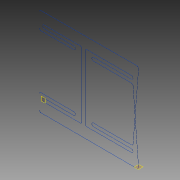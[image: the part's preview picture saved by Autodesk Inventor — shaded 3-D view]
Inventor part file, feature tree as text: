
AUTODESK INVENTOR PART (.ipt)
format: ipt  version: 2013 (Build 170138000, 138)  size: 158,208 bytes
history: native  units: in
note: dims shown in document units (in); Inventor stores cm internally (conversion verified against a paired STEP export)
features: reference x20, sketch x3, plane x2, sweep x1, extrude x1
ambient origin geometry x8: Origin, YZ Plane, XZ Plane, XY Plane, X Axis, Y Axis, Z Axis, Center Point
bodies: Solid1 (feature_tree)
feature tree (27):
  plane  "Work Plane1"
  sketch  "Sketch1"  dims[d0=-0.0984in d2=0.0197in]
  plane  "Work Plane2"
  sweep  "Sweep1"
  extrude  "Extrusion1"  Depth=0.0394in
  reference  "Reference1"
  reference  "Reference2"
  reference  "Reference3"
  reference  "Reference4"
  reference  "Reference5"
  reference  "Reference6"
  reference  "Reference7"
  reference  "Reference8"
  reference  "Reference9"
  reference  "Reference10"
  reference  "Reference11"
  reference  "Reference12"
  reference  "Reference13"
  reference  "Reference14"
  reference  "Reference15"
  reference  "Reference16"
  reference  "Reference17"
  reference  "Reference18"
  reference  "Reference19"
  reference  "Reference20"
  sketch  "Sketch2"  dims[d4=0.0197in d5=0.0394in]
  sketch  "Sketch3"  dims[d7=0.0in d8=1.0in d9=0.0in]
